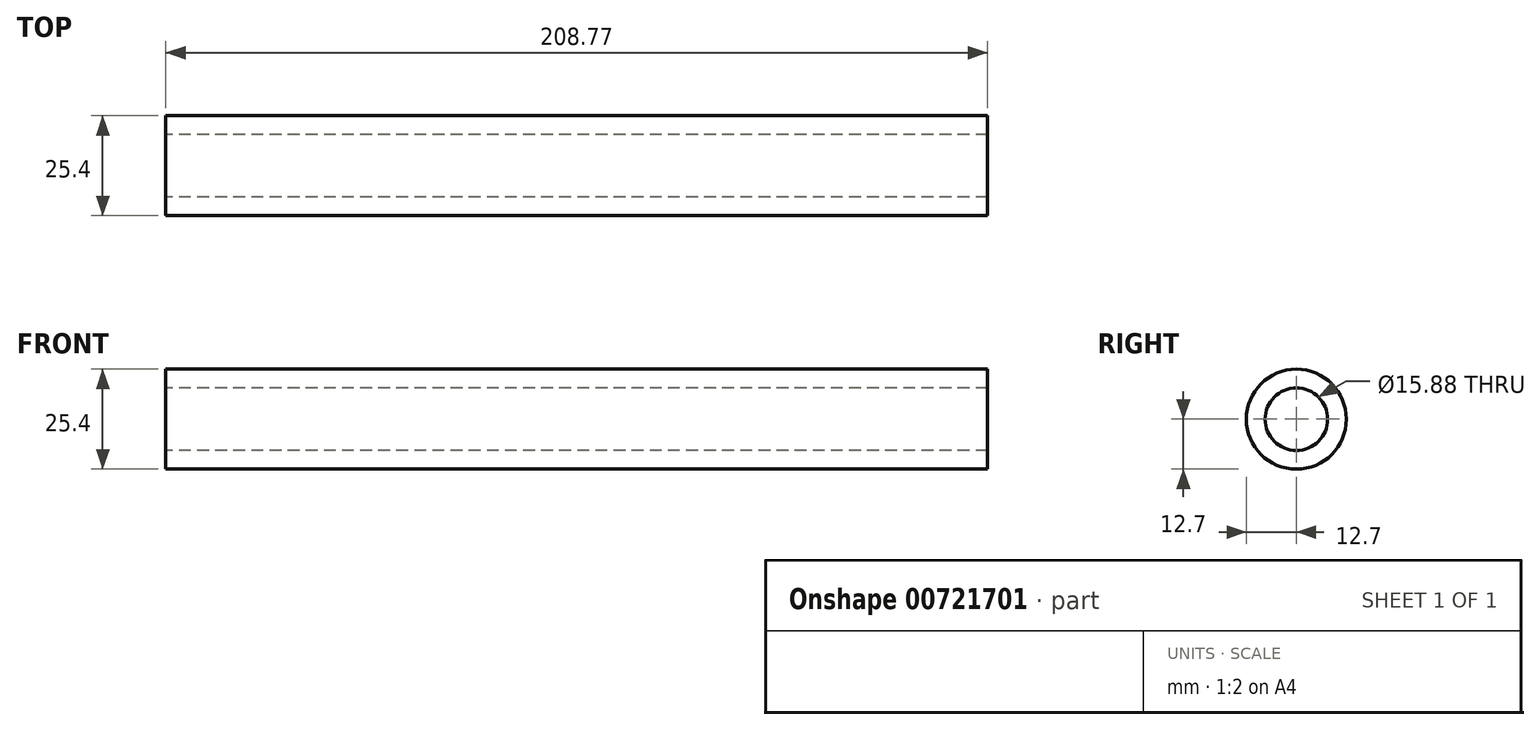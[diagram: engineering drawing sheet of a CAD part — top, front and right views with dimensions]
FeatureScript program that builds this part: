
annotation { "Feature Type Name" : "Feature", "Feature Type Description" : "" }
export const myFeature = defineFeature(function(context is Context, id is Id, definition is map)
    precondition{}
    {
        {
            var Q0;
            Q0=qCreatedBy(makeId("Front.planeOp"),FACE);
            var sketch = newSketch(context, id + "F0", { "sketchPlane" : qUnion([Q0])});
            skLineSegment(sketch, "E0", {"start": v(172.23, 0) * mm, "end": v(381, 0) * mm});
            skLineSegment(sketch, "E1", {"start": v(0, 299.62) * mm, "end": v(0, -392.92) * mm, "construction": true});
            skLineSegment(sketch, "E2", {"start": v(-101.06, 0) * mm, "end": v(111.4, 0) * mm, "construction": true});
            skPoint(sketch, "E3.visualSharp", {"position": v(4518.56, 0) * mm});
            skPoint(sketch, "E4.orphan", {"position": v(-4518.56, 0) * mm});
            skSolve(sketch);
        }
        {
            var Q0;
            Q0=qCreatedBy(makeId("Right.planeOp"),FACE);
            cPlane(context, id + "F1", {"entities" : qUnion([Q0]), "cplaneType" : CPlaneType.OFFSET, "offset" : 381 * mm, "width" : 152.4 * mm, "height" : 152.4 * mm});
        }
        {
            var Q0;
            Q0=qCreatedBy(id+"F1.planeOp",FACE);
            var sketch = newSketch(context, id + "F2", { "sketchPlane" : qUnion([Q0])});
            skCircle(sketch, "E5", {"center": v(0, 0) * mm, "radius": 12.7 * mm});
            skCircle(sketch, "E6", {"center": v(0, 0) * mm, "radius": 7.94 * mm});
            skSolve(sketch);
        }
        {
            var Q0;
            Q0=qSketchRegion(id+"F2",true);
            var Q1;
            Q1=qConstructionFilter(qBodyType(qCreatedBy(id+"F0",EDGE),BodyType.WIRE),ConstructionObject.NO);
            sweep(context, id + "F3", {"profiles" : qUnion([Q0]), "path" : qUnion([Q1])});
        }
    });
